# Revit family: powerbrik_r_0ls5297l10840_c4a5
name_source: partatom
category: Lighting Fixtures
units: mm (PartAtom-declared; Revit-internal decimal feet)

## family parameters
Cut with Voids When Loaded = No
Host = Face
Light Source = No
Part Type = Normal
Room Calculation Point = No
Round Connector Dimension = Use Diameter
Shared = No

## types (1)
- POWERBRIK® (1 x LED 4000K / CRI = 80, 900 lm, 9.5 W, 4000K)
    Apparent Load = 10 VA
    CIE Flux Codes = 45 74 92 87 100
    Color Rendering = 85
    Color Temperature = 4000K
    Default Elevation = 1800 mm
    Description = POWERBRIK®, damp-proof luminaire, primary optical cover: enclosure, of PC, primary light characteristic: symmetric, installation type: surface-mounted, LED rated luminous flux: 900 lm, light colour: 840, colour temperature: 4000K, control gear: ECG, with terminal, 2-pole, max. 1.5mm², mains connection: 230V, AC/DC, 0/50..60Hz, rated input power: 9.5W, housing, of PC, traffic white (RAL 9016), length: 160 mm, width: 90 mm, height: 50mm, protection rating (complete): IP65, insulation class (complete): insulation class II (safety insulation), certification: CE, protection symbol: F, impact resistance: IK09, permissible ambient temperature for indoor applications: -20..+40°C, packaging unit: 1 piece
    Height = 50 mm
    Lamp = 1 x LED 4000K / CRI >= 80
    Lamp Light Flux = 900 lm
    Lamp Power = 9.5 W
    Lamp count = 1
    Length = 182 mm
    Luminous efficacy = 95 lm/W
    Manufacturer = Siteco
    ModVariant = No
    Model = 0LS5297L10840
    Mounting Place = Ceiling
    Mounting Type = Surface mounted
    Number of Poles = 1
    OnlyDefault = Yes
    Power Factor = 1
    Product Name = POWERBRIK®
    Product group = damp-proof luminaire | ceiling mounted
    ProductGroupID = 300
    Protection Class = Protection class II
    Protection Degree = IP 65
    RLX_Detail_Level = 1
    RlxData = <blob elided: 48105 chars, md5=3974a7d4>
    Socket = socket
    Standby Power = 0 W
    System Light Flux = 900 lm
    System Power = 10 W
    Type Comments = Product without accessories
    Type Image = l_1006086.jpg
    URL = http://relux.com
    VarID = ---
    Voltage = 0 V
    Weight = 0.00 kg
    Width = 90 mm

## geometry (parser evidence)
native form markers: Sweep x15
no freeform markers — native parametric forms only
